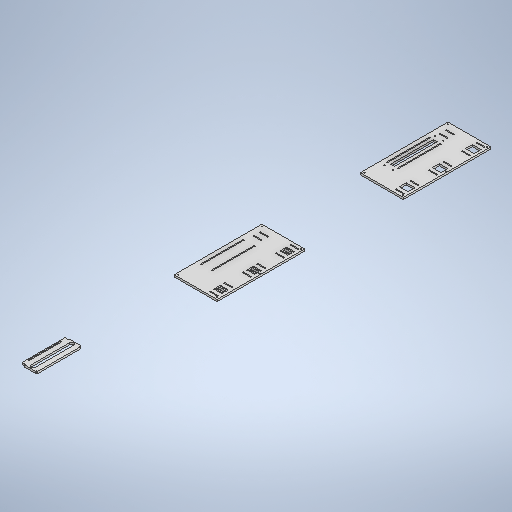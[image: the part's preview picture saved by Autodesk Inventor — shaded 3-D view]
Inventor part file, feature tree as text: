
AUTODESK INVENTOR PART (.ipt)
format: ipt  version: 2025 (Build 290162000, 162)  size: 485,376 bytes
history: native  units: in
note: dims shown in document units (in); Inventor stores cm internally (conversion verified against a paired STEP export)
features: extrude x1, sketch x1
ambient origin geometry x8: Origin, YZ Plane, XZ Plane, XY Plane, X Axis, Y Axis, Z Axis, Center Point
bodies: Solid1 (feature_tree)
feature tree (2):
  extrude  "Extrusion1"  Depth=3.5433in
  sketch  "Sketch1"  dims[d0=7.874in d1=1.5748in d2=0.1969in d3=8.6614in d4=7.874in d5=1.5748in d6=0.1969in d7=0.4724in d8=1.5748in d9=0.1969in d10=1.5748in d11=0.1969in d12=1.4173in d13=1.7717in d14=0.1969in d15=0.1969in d16=0.1969in d17=8.6614in d18=0.7874in d19=17.7165in d20=0.7874in d21=17.7165in d22=0.1969in d23=8.6614in d24=0.1969in d25=3.5433in d26=9.0551in d28=0.1969in d29=1.1811in d30=0.1969in d31=0.1969in d33=0.1969in d34=6.6929in d35=0.8661in d36=8.6614in d38=0.3937in d39=0.0in]
